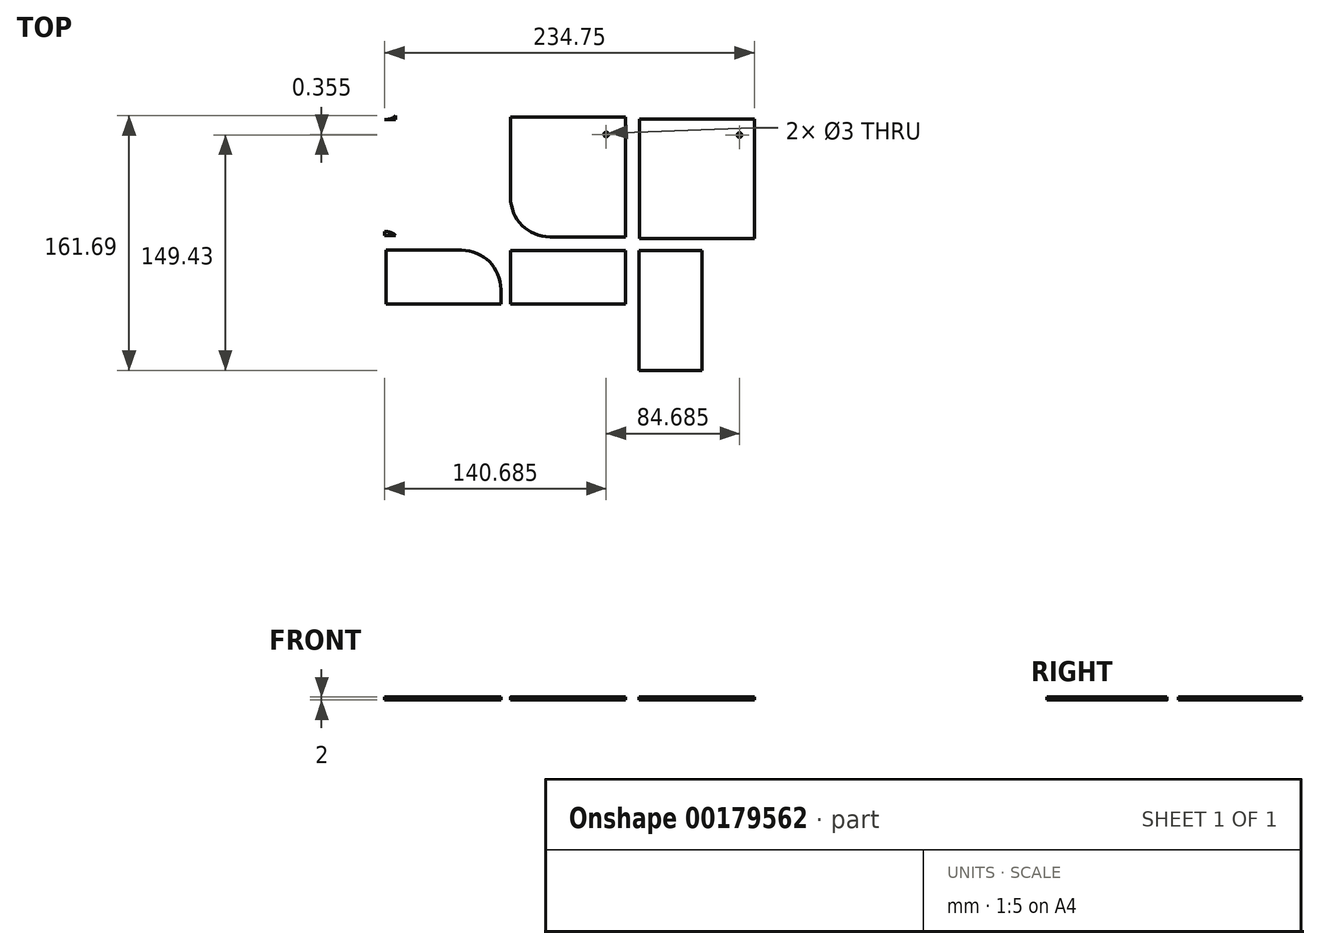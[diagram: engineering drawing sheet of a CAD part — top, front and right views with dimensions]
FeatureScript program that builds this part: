
annotation { "Feature Type Name" : "Feature", "Feature Type Description" : "" }
export const myFeature = defineFeature(function(context is Context, id is Id, definition is map)
    precondition{}
    {
        {
            var Q0;
            Q0=qCreatedBy(makeId("Top.planeOp"),FACE);
            var sketch = newSketch(context, id + "F0", { "sketchPlane" : qUnion([Q0])});
            skLineSegment(sketch, "E0.bottom", {"start": v(-79.9, 85.7) * mm, "end": v(-6.9, 85.7) * mm});
            skLineSegment(sketch, "E0.top", {"start": v(-79.9, 9.7) * mm, "end": v(-6.9, 9.7) * mm});
            skLineSegment(sketch, "E0.left", {"start": v(-79.9, 85.7) * mm, "end": v(-79.9, 9.7) * mm});
            skLineSegment(sketch, "E0.right", {"start": v(-6.9, 85.7) * mm, "end": v(-6.9, 9.7) * mm});
            skSolve(sketch);
        }
        {
            var Q0;
            Q0=qSketchRegion(id+"F0",true);
            extrude(context, id + "F1", {"entities" : qUnion([Q0]), "depth" : 2 * mm});
        }
        {
            var Q0;
            Q0=qCreatedBy(makeId("Top.planeOp"),FACE);
            var sketch = newSketch(context, id + "F2", { "sketchPlane" : qUnion([Q0])});
            skLineSegment(sketch, "E1.bottom", {"start": v(0, 84.75) * mm, "end": v(73, 84.75) * mm});
            skLineSegment(sketch, "E1.top", {"start": v(25, 8.75) * mm, "end": v(73, 8.75) * mm});
            skLineSegment(sketch, "E1.left", {"start": v(0, 84.75) * mm, "end": v(0, 33.75) * mm});
            skLineSegment(sketch, "E1.right", {"start": v(73, 84.75) * mm, "end": v(73, 8.75) * mm});
            skPoint(sketch, "E2.visualSharp", {"position": v(0, 8.75) * mm});
            skArc(sketch, "E2.filletArc", {"start": v(0, 33.75) * mm, "mid": v(7.33, 16.07) * mm, "end": v(25, 8.75) * mm});
            skSolve(sketch);
        }
        {
            var Q0;
            Q0=qSketchRegion(id+"F2",true);
            extrude(context, id + "F3", {"entities" : qUnion([Q0]), "depth" : 2 * mm});
        }
        {
            var Q0;
            Q0=qCreatedBy(makeId("Top.planeOp"),FACE);
            var sketch = newSketch(context, id + "F4", { "sketchPlane" : qUnion([Q0])});
            skLineSegment(sketch, "E3.bottom", {"start": v(-79.15, 0.26) * mm, "end": v(-31.15, 0.26) * mm});
            skLineSegment(sketch, "E3.top", {"start": v(-79.15, -33.74) * mm, "end": v(-6.15, -33.74) * mm});
            skLineSegment(sketch, "E3.left", {"start": v(-79.15, 0.26) * mm, "end": v(-79.15, -33.74) * mm});
            skLineSegment(sketch, "E3.right", {"start": v(-6.15, -24.74) * mm, "end": v(-6.15, -33.74) * mm});
            skPoint(sketch, "E4.visualSharp", {"position": v(-6.15, 0.26) * mm});
            skArc(sketch, "E4.filletArc", {"start": v(-6.15, -24.74) * mm, "mid": v(-13.47, -7.06) * mm, "end": v(-31.15, 0.26) * mm});
            skSolve(sketch);
        }
        {
            var Q0;
            Q0=qSketchRegion(id+"F4",true);
            extrude(context, id + "F5", {"entities" : qUnion([Q0]), "depth" : 2 * mm});
        }
        {
            var Q0;
            Q0=qCreatedBy(makeId("Top.planeOp"),FACE);
            var sketch = newSketch(context, id + "F6", { "sketchPlane" : qUnion([Q0])});
            skLineSegment(sketch, "E5.bottom", {"start": v(0.04, 0) * mm, "end": v(73.04, 0) * mm});
            skLineSegment(sketch, "E5.top", {"start": v(0.04, -34) * mm, "end": v(73.04, -34) * mm});
            skLineSegment(sketch, "E5.left", {"start": v(0.04, 0) * mm, "end": v(0.04, -34) * mm});
            skLineSegment(sketch, "E5.right", {"start": v(73.04, 0) * mm, "end": v(73.04, -34) * mm});
            skSolve(sketch);
        }
        {
            var Q0;
            Q0=qSketchRegion(id+"F6",true);
            extrude(context, id + "F7", {"entities" : qUnion([Q0]), "depth" : 2 * mm});
        }
        {
            var Q0;
            Q0=qCreatedBy(makeId("Top.planeOp"),FACE);
            var sketch = newSketch(context, id + "F8", { "sketchPlane" : qUnion([Q0])});
            skLineSegment(sketch, "E6.bottom", {"start": v(81.84, 83.66) * mm, "end": v(154.84, 83.66) * mm});
            skLineSegment(sketch, "E6.top", {"start": v(81.84, 7.66) * mm, "end": v(154.84, 7.66) * mm});
            skLineSegment(sketch, "E6.left", {"start": v(81.84, 83.66) * mm, "end": v(81.84, 7.66) * mm});
            skLineSegment(sketch, "E6.right", {"start": v(154.84, 83.66) * mm, "end": v(154.84, 7.66) * mm});
            skSolve(sketch);
        }
        {
            var Q0;
            Q0=makeQuery(id+"F8.imprint","IMPRINT",FACE,{"disambiguationData":[TD([[makeQuery(id+"F8.imprint","IMPRINT",EDGE,{"derivedFrom":sQuery(id+"F8.wireOp",EDGE,"E6.bottom")}),-1.0]])]});
            extrude(context, id + "F9", {"entities" : qUnion([Q0]), "depth" : 2 * mm});
        }
        {
            var Q0;
            Q0=qCreatedBy(makeId("Top.planeOp"),FACE);
            var sketch = newSketch(context, id + "F10", { "sketchPlane" : qUnion([Q0])});
            skLineSegment(sketch, "E7.bottom", {"start": v(121.44, 0) * mm, "end": v(121.44, -76) * mm});
            skLineSegment(sketch, "E7.top", {"start": v(81.44, 0) * mm, "end": v(81.44, -76) * mm});
            skLineSegment(sketch, "E7.left", {"start": v(121.44, 0) * mm, "end": v(81.44, 0) * mm});
            skLineSegment(sketch, "E7.right", {"start": v(121.44, -76) * mm, "end": v(81.44, -76) * mm});
            skLineSegment(sketch, "E8.bottom", {"start": v(168.25, 0) * mm, "end": v(168.25, -76) * mm});
            skLineSegment(sketch, "E8.top", {"start": v(128.25, 0) * mm, "end": v(128.25, -76) * mm});
            skLineSegment(sketch, "E8.left", {"start": v(168.25, 0) * mm, "end": v(128.25, 0) * mm});
            skLineSegment(sketch, "E8.right", {"start": v(168.25, -76) * mm, "end": v(128.25, -76) * mm});
            skSolve(sketch);
        }
        {
            var Q0;
            Q0=qSketchRegion(id+"F10",true);
            extrude(context, id + "F11", {"entities" : qUnion([Q0]), "depth" : 2 * mm});
        }
        {
            var Q0;
            Q0=makeQuery(id+"F11.opExtrude","SWEPT_BODY",BODY,{"disambiguationData":[OSD([sQuery(id+"F10.wireOp",EDGE,"E8.bottom"),sQuery(id+"F10.wireOp",EDGE,"E8.top"),sQuery(id+"F10.wireOp",EDGE,"E8.left"),sQuery(id+"F10.wireOp",EDGE,"E8.right")])]});
            deleteBodies(context, id + "F12", {"entities" : qUnion([Q0])});
        }
        {
            var Q0;
            Q0=makeQuery(id+"F1.opExtrude","CAP_FACE",FACE,{"disambiguationData":[OSD([sQuery(id+"F0.wireOp",EDGE,"E0.bottom"),sQuery(id+"F0.wireOp",EDGE,"E0.top"),sQuery(id+"F0.wireOp",EDGE,"E0.left"),sQuery(id+"F0.wireOp",EDGE,"E0.right")])],"isStart":false});
            var sketch = newSketch(context, id + "F13", { "sketchPlane" : qUnion([Q0])});
            skCircle(sketch, "E9", {"center": v(-13.9, 16.7) * mm, "radius": 1.5 * mm});
            skCircle(sketch, "E10", {"center": v(-43.9, 76.7) * mm, "radius": 1.5 * mm});
            skCircle(sketch, "E11", {"center": v(60.77, 73.78) * mm, "radius": 1.5 * mm});
            skCircle(sketch, "E12", {"center": v(145.46, 73.43) * mm, "radius": 1.5 * mm});
            skLineSegment(sketch, "E13", {"start": v(-43.9, 76.7) * mm, "end": v(-43.9, 85.7) * mm, "construction": true});
            skLineSegment(sketch, "E14", {"start": v(-43.9, 76.7) * mm, "end": v(-6.9, 76.7) * mm, "construction": true});
            skLineSegment(sketch, "E15", {"start": v(-13.9, 16.7) * mm, "end": v(-13.9, 9.7) * mm, "construction": true});
            skLineSegment(sketch, "E16", {"start": v(-13.9, 16.7) * mm, "end": v(-6.9, 16.7) * mm, "construction": true});
            skLineSegment(sketch, "E17", {"start": v(60.77, 73.78) * mm, "end": v(72.77, 73.78) * mm, "construction": true});
            skLineSegment(sketch, "E18", {"start": v(145.46, 73.43) * mm, "end": v(154.46, 73.43) * mm, "construction": true});
            skLineSegment(sketch, "E19", {"start": v(145.46, 73.43) * mm, "end": v(145.46, 83.43) * mm, "construction": true});
            skSolve(sketch);
        }
        {
            var Q0;
            Q0=makeQuery(id+"F13.imprint","IMPRINT",FACE,{"disambiguationData":[TD([[makeQuery(id+"F13.imprint","IMPRINT",EDGE,{"derivedFrom":sQuery(id+"F13.wireOp",EDGE,"E11")}),1.0]])]});
            var Q1;
            Q1=makeQuery(id+"F13.imprint","IMPRINT",FACE,{"disambiguationData":[TD([[makeQuery(id+"F13.imprint","IMPRINT",EDGE,{"derivedFrom":sQuery(id+"F13.wireOp",EDGE,"E12")}),1.0]])]});
            var Q2;
            Q2=makeQuery(id+"F13.imprint","IMPRINT",FACE,{"disambiguationData":[TD([[makeQuery(id+"F13.imprint","IMPRINT",EDGE,{"derivedFrom":sQuery(id+"F13.wireOp",EDGE,"E9")}),1.0]])]});
            var Q3;
            Q3=makeQuery(id+"F13.imprint","IMPRINT",FACE,{"disambiguationData":[TD([[makeQuery(id+"F13.imprint","IMPRINT",EDGE,{"derivedFrom":sQuery(id+"F13.wireOp",EDGE,"E10")}),1.0]])]});
            var Q4;
            Q4=qConstructionFilter(qBodyType(qCreatedBy(id+"F13",EDGE),BodyType.WIRE),ConstructionObject.NO);
            extrude(context, id + "F14", {"entities" : qUnion([Q0, Q1, Q2, Q3]), "operationType" : NewBodyOperationType.REMOVE, "surfaceEntities" : qUnion([Q4]), "oppositeDirection" : true, "depth" : 3 * mm});
        }
        {
            var Q0;
            Q0=makeQuery(id+"F1.opExtrude","CAP_FACE",FACE,{"disambiguationData":[OSD([sQuery(id+"F0.wireOp",EDGE,"E0.bottom"),sQuery(id+"F0.wireOp",EDGE,"E0.top"),sQuery(id+"F0.wireOp",EDGE,"E0.left"),sQuery(id+"F0.wireOp",EDGE,"E0.right")])],"isStart":false});
            var sketch = newSketch(context, id + "F15", { "sketchPlane" : qUnion([Q0])});
            skLineSegment(sketch, "E20", {"start": v(-79.9, 85.7) * mm, "end": v(-79.9, 83.2) * mm});
            skLineSegment(sketch, "E21", {"start": v(-79.9, 83.2) * mm, "end": v(-72.9, 83.2) * mm});
            skLineSegment(sketch, "E22", {"start": v(-72.9, 83.2) * mm, "end": v(-72.9, 85.7) * mm});
            skLineSegment(sketch, "E23", {"start": v(-72.9, 85.7) * mm, "end": v(-79.9, 85.7) * mm});
            skArc(sketch, "E24", {"start": v(-79.9, 83.2) * mm, "mid": v(-76.19, 83.84) * mm, "end": v(-72.9, 85.7) * mm});
            skLineSegment(sketch, "E25", {"start": v(-79.9, 47.7) * mm, "end": v(-6.9, 47.7) * mm, "construction": true});
            skArc(sketch, "E26.MirrorCS", {"start": v(-79.9, 12.2) * mm, "mid": v(-76.19, 11.55) * mm, "end": v(-72.9, 9.7) * mm});
            skLineSegment(sketch, "E27.MirrorCS", {"start": v(-72.9, 9.7) * mm, "end": v(-79.9, 9.7) * mm});
            skLineSegment(sketch, "E28.MirrorCS", {"start": v(-79.9, 9.7) * mm, "end": v(-79.9, 12.2) * mm});
            skSolve(sketch);
        }
        {
            var Q0;
            Q0=makeQuery(id+"F15.imprint","IMPRINT",FACE,{"disambiguationData":[TD([[makeQuery(id+"F15.imprint","IMPRINT",EDGE,{"derivedFrom":sQuery(id+"F15.wireOp",EDGE,"E20")}),1.0]])]});
            var Q1;
            Q1=makeQuery(id+"F15.imprint","IMPRINT",FACE,{"disambiguationData":[TD([[makeQuery(id+"F15.imprint","IMPRINT",EDGE,{"derivedFrom":sQuery(id+"F15.wireOp",EDGE,"E26.MirrorCS")}),-1.0]])]});
            extrude(context, id + "F16", {"entities" : qUnion([Q0, Q1]), "operationType" : NewBodyOperationType.REMOVE, "oppositeDirection" : true, "depth" : 25 * mm, "offsetDistance" : 25 * mm});
        }
    });
